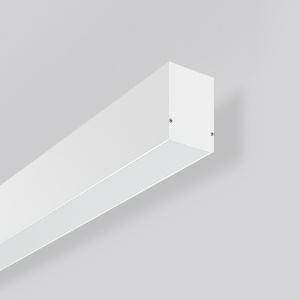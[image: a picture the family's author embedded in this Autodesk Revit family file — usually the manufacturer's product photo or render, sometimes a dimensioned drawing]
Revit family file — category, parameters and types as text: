
# Revit family: less_is_more_50_312612_002_76_307f
name_source: partatom
category: Lighting Fixtures
units: mm (PartAtom-declared; Revit-internal decimal feet)

## family parameters
Cut with Voids When Loaded = No
Host = Face
Light Source = No
Part Type = Normal
Room Calculation Point = No
Round Connector Dimension = Use Diameter
Shared = No

## types (1)
- LESS IS MORE 50 (1 x LED Modul 830, 3900 lm, 3000)
    Apparent Load = 30 VA
    CIE Flux Codes = 48 80 96 50 100
    Color Rendering = 80
    Color Temperature = 3000
    Default Elevation = 1800 mm
    Description = Series: LESS IS MORE 50
Linear wall luminaires. Housing: extruded aluminium profile, powder-coated. End cap aluminium powder-coated. Diffuser made of non-yellowing plastic (PMMA), opal. Direct 50%, indirect 50% light emission. Suitable for Wall (surface). LED unit with integrated converter interchangeable and removable. Suitable for through-wiring. With sensors or as a safety luminaire on request. 
Colour: traffic white, matt (RAL 9016)
Length: 1687 mm
Width: 67 mm
Height: 75 mm
Lamp: LED
Socket: without socket
Colour temperature: 3000K
Colour rendering index (CRI): 80
Light source: LED
Socket lamp2: Without base
Colour temperature: 3000K
Colour rendering index (CRI) 2: 80
System power: 30 W
Rated luminous flux: 3900 lm
Luminous efficiency: 130 lm/W
Control gear: Converter, dimmable, DALI
Control gear: Converter, dimmable, DALI
Protection class: I
Type of protection: IP 20
    Height = 75 mm
    Lamp = 1 x LED Modul 830
    Lamp Light Flux = 3900 lm
    Lamp count = 1
    Length = 1687 mm
    Lifetime = 50000 h
    Luminous efficacy = 130 lm/W
    Manufacturer = RZB
    ModVariant = No
    Model = 312612.002.76
    Mounting Place = Wall
    Mounting Type = Surface mounted
    Number of Poles = 1
    OnlyDefault = Yes
    Power Factor = 1
    Product Name = LESS IS MORE 50
    Product group = Surface mounted LED linear luminaires
    ProductGroupID = 2007
    Protection Class = Protection class I
    Protection Degree = IP 20
    RLX_Detail_Level = 1
    RLX_Emergency_Light_Flux = 0 lm
    RLX_Emergency_Type = 0
    RLX_Emergency_Type_DB = No
    RlxData = <blob elided: 39613 chars, md5=b5ecaa7f>
    Socket = socket
    Standby Power = 0 W
    System Light Flux = 3900 lm
    System Power = 30 W
    Type Comments = Product without accessories
    Type Image = 312606.002.jpg
    URL = http://relux.com
    VarID = ---
    Voltage = 0 V
    Weight = 0.00 kg
    Width = 67 mm

## geometry (parser evidence)
native form markers: Blend x4, Sweep x14
no freeform markers — native parametric forms only
